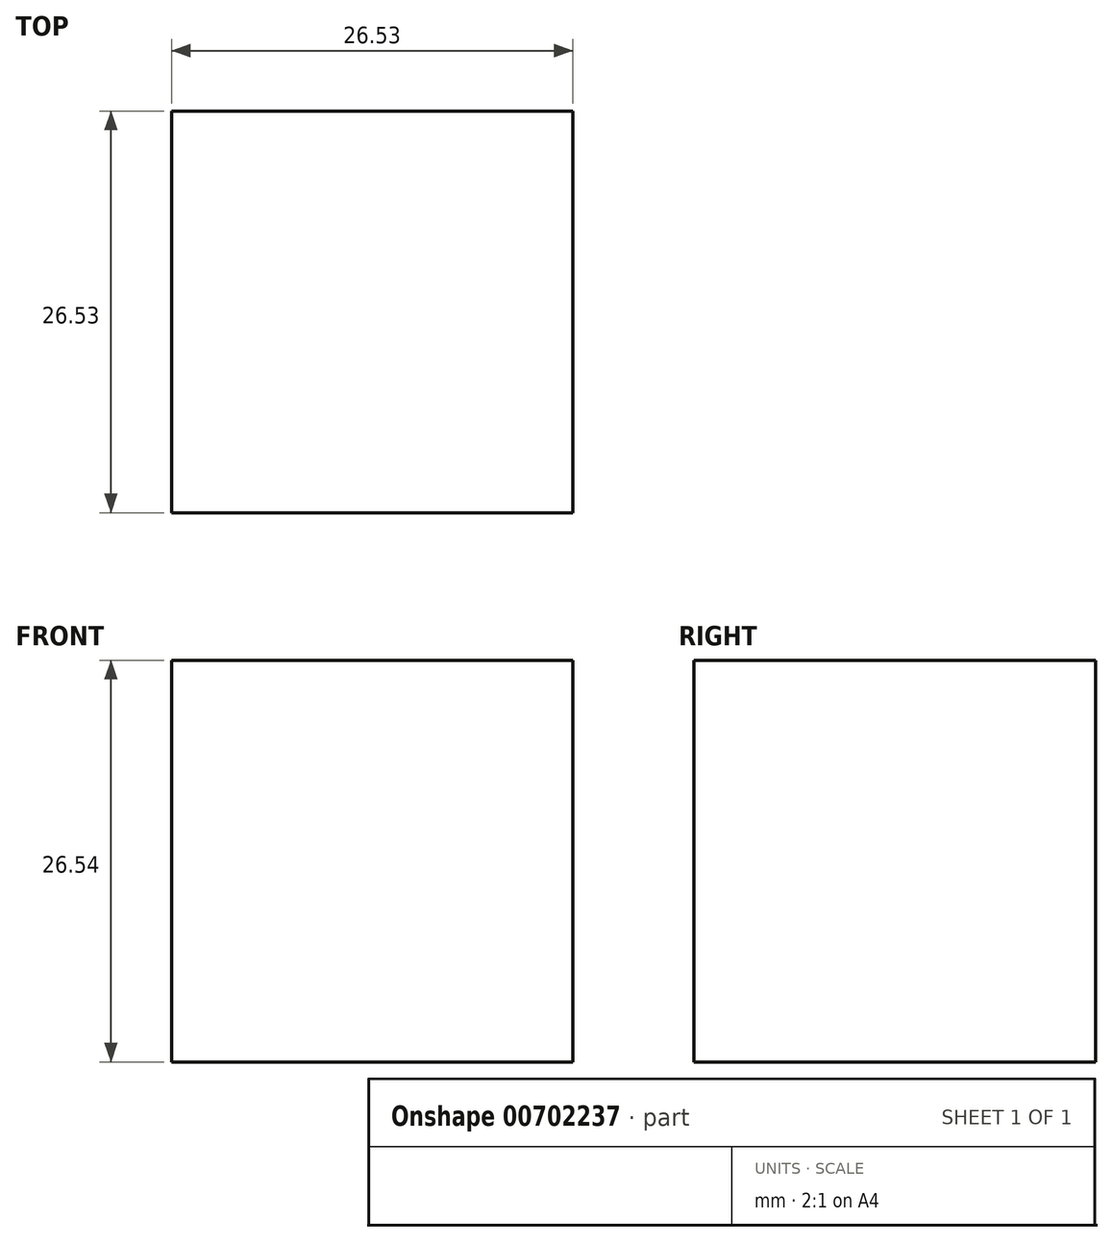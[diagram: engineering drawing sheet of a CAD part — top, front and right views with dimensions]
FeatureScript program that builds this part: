
annotation { "Feature Type Name" : "Feature", "Feature Type Description" : "" }
export const myFeature = defineFeature(function(context is Context, id is Id, definition is map)
    precondition{}
    {
        {
            var Q0;
            Q0=qCreatedBy(makeId("Top.planeOp"),FACE);
            var sketch = newSketch(context, id + "F0", { "sketchPlane" : qUnion([Q0])});
            skLineSegment(sketch, "E0.bottom", {"start": v(0, 0) * mm, "end": v(26.53, 0) * mm});
            skLineSegment(sketch, "E0.top", {"start": v(0, 26.53) * mm, "end": v(26.53, 26.53) * mm});
            skLineSegment(sketch, "E0.left", {"start": v(0, 0) * mm, "end": v(0, 26.53) * mm});
            skLineSegment(sketch, "E0.right", {"start": v(26.53, 0) * mm, "end": v(26.53, 26.53) * mm});
            skSolve(sketch);
        }
        {
            var Q0;
            Q0=makeQuery(id+"F0.imprint","IMPRINT",FACE,{"disambiguationData":[TD([[makeQuery(id+"F0.imprint","IMPRINT",EDGE,{"derivedFrom":sQuery(id+"F0.wireOp",EDGE,"E0.bottom")}),1.0]])]});
            extrude(context, id + "F1", {"entities" : qUnion([Q0]), "depth" : 26.54 * mm, "offsetDistance" : 25.4 * mm});
        }
    });
